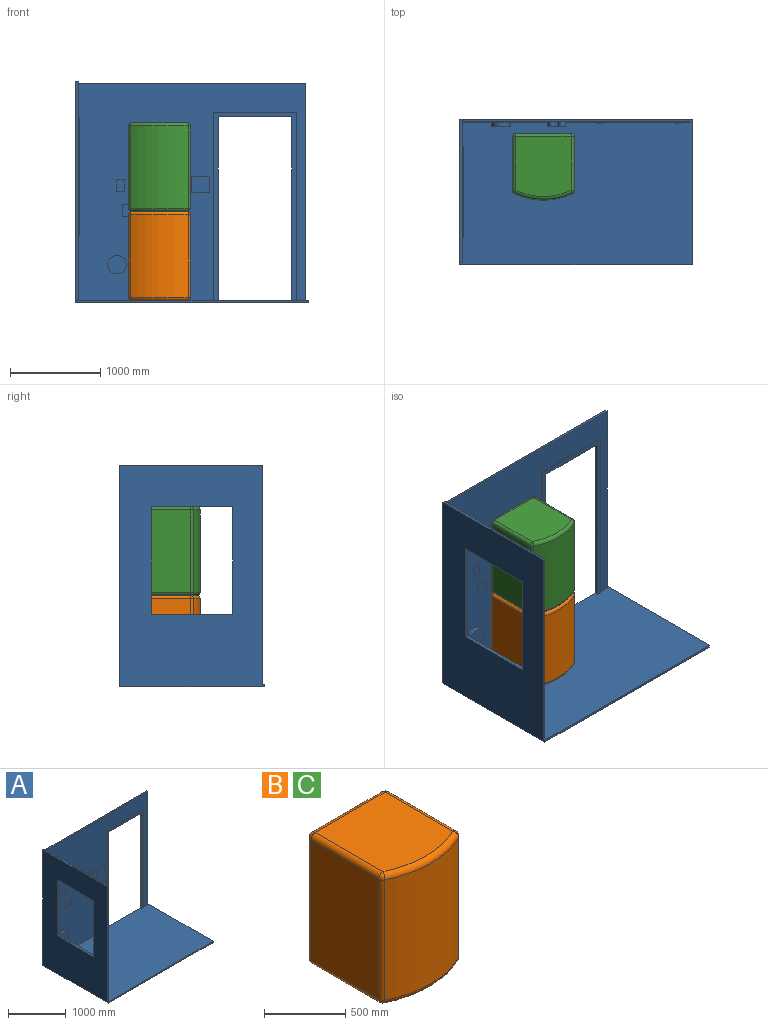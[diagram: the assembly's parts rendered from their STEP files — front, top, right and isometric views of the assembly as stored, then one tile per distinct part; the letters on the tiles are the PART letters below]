
ASSEMBLY  parts=3 mates=2
PART A: 51 faces, bbox 2571.1x1600.2x2451.1 mm
  f0: plane 1574.8x25.4mm, normal (0,0,1), area 39999.9mm2, adj f1,f2,f3,f15
  f1: plane 2425.7x25.4mm, normal (0,-1,0), area 61612.8mm2, adj f0,f2,f3,f47
  f2: plane 2451.1x1600.2mm, normal (-1,0,0), area 2784188mm2, adj f0,f1,f7,f8,f9,f10,f15,f47
  f3: plane 2425.7x1574.8mm, normal (1,0,0), area 2459349.9mm2, adj f0,f1,f4,f5,f6,f11,f14,f15
  f4: plane 1003.3x12.7mm, normal (0,0,-1), area 12741.9mm2, adj f3,f5,f11,f12
  f5: plane 1295.4x12.7mm, normal (0,1,0), area 16451.6mm2, adj f3,f4,f6,f12
  f6: plane 1003.3x12.7mm, normal (0,0,1), area 12741.9mm2, adj f3,f5,f11,f12
  f7: plane 901.7x38.1mm, normal (0,0,-1), area 34354.8mm2, adj f2,f8,f10,f12
  f8: plane 1193.8x38.1mm, normal (0,-1,0), area 45483.8mm2, adj f2,f7,f9,f12
  f9: plane 901.7x38.1mm, normal (0,0,1), area 34354.8mm2, adj f2,f8,f10,f12
  f10: plane 1193.8x38.1mm, normal (0,1,0), area 45483.8mm2, adj f2,f7,f9,f12
  f11: plane 1295.4x12.7mm, normal (0,-1,0), area 16451.6mm2, adj f3,f4,f6,f12
  f12: plane 1295.4x1003.3mm, normal (1,0,0), area 223225.4mm2, adj f4,f5,f6,f7,f8,f9,f10,f11
  f13: plane 2400.3x25.4mm, normal (1,0,0), area 60967.6mm2, adj f14,f15,f16,f47
  f14: plane 2520.32x25.4mm, normal (0,0,1), area 64016.1mm2, adj f3,f13,f15,f16
  f15: plane 2571.12x2451.1mm, normal (0,1,0), area 4524831.1mm2, adj f0,f2,f3,f13,f14,f17,f21,f22
  f16: plane 2520.32x2400.3mm, normal (0,-1,0), area 4029864mm2, adj f3,f13,f14,f18,f19,f20,f24,f26
  f17: plane 2032x38.1mm, normal (-1,0,0), area 77419.2mm2, adj f15,f22,f23,f47
  f18: plane 2082.8x12.7mm, normal (1,0,0), area 26451.6mm2, adj f16,f19,f23,f47
  f19: plane 914.4x12.7mm, normal (0,0,1), area 11612.9mm2, adj f16,f18,f20,f23
  f20: plane 2082.8x12.7mm, normal (-1,0,0), area 26451.6mm2, adj f16,f19,f23,f47
  f21: plane 2032x38.1mm, normal (1,0,0), area 77419.2mm2, adj f15,f22,f23,f47
  f22: plane 812.8x38.1mm, normal (0,0,-1), area 30967.7mm2, adj f15,f17,f21,f23
  f23: plane 2082.8x914.4mm, normal (0,-1,0), area 252902.7mm2, adj f17,f18,f19,f20,f21,f22,f47
  f24: cylinder r=41.59mm len=83.18mm, axis (0,1,0), area 13275.3mm2, adj f16,f25
  f25: plane 83.18x83.18mm, normal (0,-1,0), area 5434.4mm2, adj f24
  f26: cylinder r=41.59mm len=83.18mm, axis (0,1,0), area 13275.3mm2, adj f16,f27
  f27: plane 83.18x83.18mm, normal (0,-1,0), area 5434.4mm2, adj f26
  f28: cylinder r=54.98mm len=109.97mm, axis (0,1,0), area 17549.6mm2, adj f16,f29
  f29: plane 109.97x109.97mm, normal (0,-1,0), area 9497.3mm2, adj f28
  f30: cylinder r=103.2mm len=206.4mm, axis (0,1,0), area 32940mm2, adj f16,f31
  f31: plane 206.4x206.4mm, normal (0,-1,0), area 33458.8mm2, adj f30
  f32: plane 194.39x6.35mm, normal (0,0,1), area 1234.4mm2, adj f16,f33,f35,f36
  f33: plane 167.48x6.35mm, normal (-1,0,0), area 1063.5mm2, adj f16,f32,f34,f36
  f34: plane 194.39x6.35mm, normal (0,0,-1), area 1234.4mm2, adj f16,f33,f35,f36
  f35: plane 167.48x6.35mm, normal (1,0,0), area 1063.5mm2, adj f16,f32,f34,f36
  f36: plane 194.39x167.48mm, normal (0,-1,0), area 32556.3mm2, adj f32,f33,f34,f35
  f37: plane 140.56x6.35mm, normal (0,0,-1), area 892.6mm2, adj f16,f38,f40,f41
  f38: plane 131.59x6.35mm, normal (1,0,0), area 835.6mm2, adj f16,f37,f39,f41
  f39: plane 140.56x6.35mm, normal (0,0,1), area 892.6mm2, adj f16,f38,f40,f41
  f40: plane 131.59x6.35mm, normal (-1,0,0), area 835.6mm2, adj f16,f37,f39,f41
  f41: plane 140.56x131.59mm, normal (0,-1,0), area 18496.2mm2, adj f37,f38,f39,f40
  f42: plane 83.74x6.35mm, normal (0,0,-1), area 531.7mm2, adj f16,f43,f45,f46
  f43: plane 122.62x6.35mm, normal (1,0,0), area 778.6mm2, adj f16,f42,f44,f46
  f44: plane 83.74x6.35mm, normal (0,0,1), area 531.7mm2, adj f16,f43,f45,f46
  f45: plane 122.62x6.35mm, normal (-1,0,0), area 778.6mm2, adj f16,f42,f44,f46
  f46: plane 122.62x83.74mm, normal (0,-1,0), area 10267.7mm2, adj f42,f43,f44,f45
  f47: plane 2571.12x1600.2mm, normal (0,0,1), area 4029643.2mm2, adj f1,f2,f3,f13,f15,f16,f17,f18
  f48: plane 2571.12x25.4mm, normal (0,-1,0), area 65306.4mm2, adj f2,f47,f49,f50
  f49: plane 1600.2x25.4mm, normal (1,0,0), area 40645.1mm2, adj f15,f47,f48,f50
  f50: plane 2571.12x1600.2mm, normal (0,0,-1), area 4114304.5mm2, adj f2,f15,f48,f49
PART B: 26 faces, bbox 695.7x797.5x984.3 mm
  f0: plane 908.05x590.74mm, normal (-1,0,0), area 536418.9mm2, adj f6,f9,f13,f14
  f1: cylinder r=739.74mm len=908.05mm, axis (0,0,-1), area 603721.7mm2, adj f14,f19,f22,f25
  f2: plane 908.05x590.74mm, normal (1,0,0), area 536418.9mm2, adj f11,f20,f21,f25
  f3: plane 908.05x609.6mm, normal (0,1,0), area 553547.3mm2, adj f6,f10,f11,f12
  f4: plane 660.4x609.6mm, normal (0,0,1), area 388718mm2, adj f9,f10,f19,f20
  f5: plane 660.4x609.6mm, normal (0,0,-1), area 388718mm2, adj f12,f13,f21,f22
  f6: cylinder r=38.1mm len=908.05mm, axis (0,0,-1), area 54344.4mm2, adj f0,f3,f7,f8
  f7: sphere r=38.1mm, area 2280.2mm2, adj f6,f9,f10
  f8: sphere r=38.1mm, area 2280.2mm2, adj f6,f12,f13
  f9: cylinder r=38.1mm len=590.74mm, axis (0,1,0), area 35354mm2, adj f0,f4,f7,f15
  f10: cylinder r=38.1mm len=609.6mm, axis (1,0,0), area 36482.9mm2, adj f3,f4,f7,f16
  f11: cylinder r=38.1mm len=908.05mm, axis (0,0,1), area 54344.4mm2, adj f2,f3,f16,f17
  f12: cylinder r=38.1mm len=609.6mm, axis (-1,0,0), area 36482.9mm2, adj f3,f5,f8,f17
  f13: cylinder r=38.1mm len=590.74mm, axis (0,-1,0), area 35354mm2, adj f0,f5,f8,f18
  f14: cylinder r=38.1mm len=908.05mm, axis (0,0,-1), area 38797.1mm2, adj f0,f1,f15,f18
  f15: sphere r=38.1mm, area 1627.8mm2, adj f9,f14,f19
  f16: sphere r=38.1mm, area 2280.2mm2, adj f10,f11,f20
  f17: sphere r=38.1mm, area 2280.2mm2, adj f11,f12,f21
  f18: sphere r=38.1mm, area 1627.8mm2, adj f13,f14,f22
  f19: torus R=701.64mm, axis (0,0,1), area 39045.1mm2, adj f1,f4,f15,f23
  f20: cylinder r=38.1mm len=590.74mm, axis (0,-1,0), area 35354mm2, adj f2,f4,f16,f23
  f21: cylinder r=38.1mm len=590.74mm, axis (0,1,0), area 35354mm2, adj f2,f5,f17,f24
  f22: torus R=701.64mm, axis (0,0,1), area 39045.1mm2, adj f1,f5,f18,f24
  f23: sphere r=38.1mm, area 1627.8mm2, adj f19,f20,f25
  f24: sphere r=38.1mm, area 1627.8mm2, adj f21,f22,f25
  f25: cylinder r=38.1mm len=908.05mm, axis (0,0,-1), area 38797.1mm2, adj f1,f2,f23,f24
PART C: same geometry as B
PLACE A at identity
PLACE B t=(900.22,-453.66,0)mm
PLACE C t=(900.22,-453.66,984.25)mm
MATE fastened C.f5 <-> B.f4  axis (0,0,-1) through (900.22,-484.76,984.25)mm
MATE planar B.f5 <-> A.f47  axis (0,0,-1) through (1205.02,-460.97,0)mm
